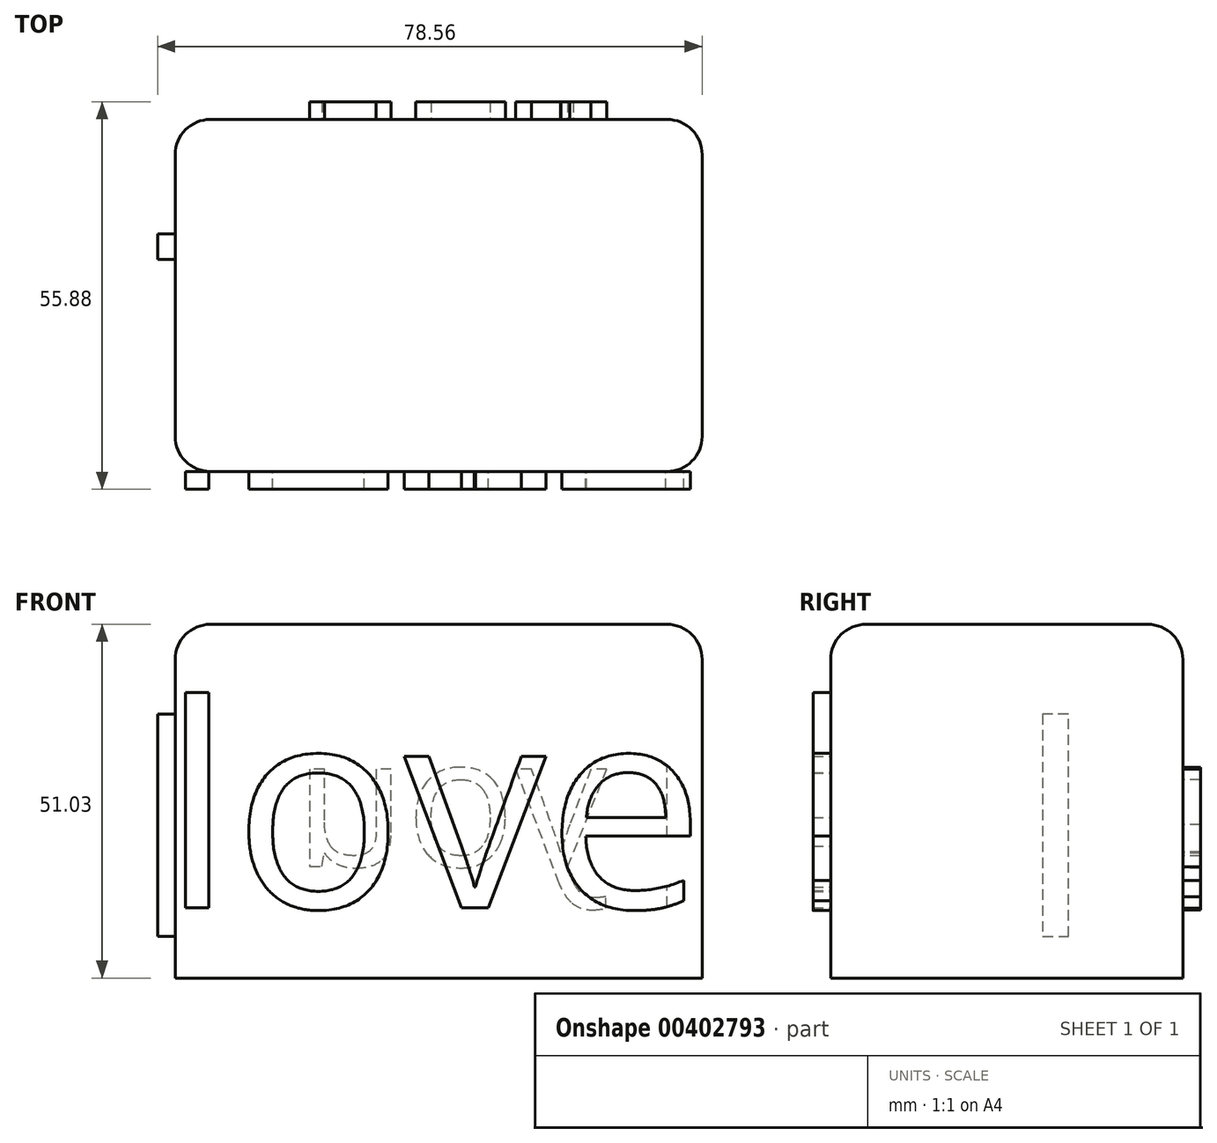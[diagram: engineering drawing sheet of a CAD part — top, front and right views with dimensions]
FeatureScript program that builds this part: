
annotation { "Feature Type Name" : "Feature", "Feature Type Description" : "" }
export const myFeature = defineFeature(function(context is Context, id is Id, definition is map)
    precondition{}
    {
        {
            var Q0;
            Q0=qCreatedBy(makeId("Front.planeOp"),FACE);
            var sketch = newSketch(context, id + "F0", { "sketchPlane" : qUnion([Q0])});
            skLineSegment(sketch, "E0.bottom", {"start": v(0, 0) * mm, "end": v(76.02, 0) * mm});
            skLineSegment(sketch, "E0.top", {"start": v(0, 51.03) * mm, "end": v(76.02, 51.03) * mm});
            skLineSegment(sketch, "E0.left", {"start": v(0, 0) * mm, "end": v(0, 51.03) * mm});
            skLineSegment(sketch, "E0.right", {"start": v(76.02, 0) * mm, "end": v(76.02, 51.03) * mm});
            skSolve(sketch);
        }
        {
            var Q0;
            Q0=makeQuery(id+"F0.imprint","IMPRINT",FACE,{"disambiguationData":[TD([[makeQuery(id+"F0.imprint","IMPRINT",EDGE,{"derivedFrom":sQuery(id+"F0.wireOp",EDGE,"E0.bottom")}),1.0]])]});
            extrude(context, id + "F1", {"entities" : qUnion([Q0]), "depth" : 50.8 * mm});
        }
        {
            var Q0;
            Q0=makeQuery(id+"F1.opExtrude","CAP_EDGE",EDGE,{"disambiguationData":[OSD([sQuery(id+"F0.wireOp",EDGE,"E0.top")])],"isStart":false});
            fillet(context, id + "F2", {"entities" : qUnion([Q0]), "radius" : 5.08 * mm, "tangentPropagation" : true, "allowEdgeOverflow" : false});
        }
        {
            var Q0;
            Q0=makeQuery(id+"F1.opExtrude","SWEPT_EDGE",EDGE,{"disambiguationData":[OSD([sQuery(id+"F0.wireOp",EDGE,"E0.top"),sQuery(id+"F0.wireOp",EDGE,"E0.right")])]});
            fillet(context, id + "F3", {"entities" : qUnion([Q0]), "radius" : 5.08 * mm, "tangentPropagation" : true, "allowEdgeOverflow" : false});
        }
        {
            var Q0;
            Q0=makeQuery(id+"F1.opExtrude","CAP_EDGE",EDGE,{"disambiguationData":[OSD([sQuery(id+"F0.wireOp",EDGE,"E0.top")])],"isStart":true});
            fillet(context, id + "F4", {"entities" : qUnion([Q0]), "radius" : 5.08 * mm, "tangentPropagation" : true, "allowEdgeOverflow" : false});
        }
        {
            var Q0;
            Q0=makeQuery(id+"F1.opExtrude","SWEPT_EDGE",EDGE,{"disambiguationData":[OSD([sQuery(id+"F0.wireOp",EDGE,"E0.top"),sQuery(id+"F0.wireOp",EDGE,"E0.left")])]});
            fillet(context, id + "F5", {"entities" : qUnion([Q0]), "radius" : 5.08 * mm, "tangentPropagation" : true, "allowEdgeOverflow" : false});
        }
        {
            var Q0;
            Q0=makeQuery(id+"F1.opExtrude","SWEPT_FACE",FACE,{"disambiguationData":[OSD([sQuery(id+"F0.wireOp",EDGE,"E0.left")])]});
            var sketch = newSketch(context, id + "F6", { "sketchPlane" : qUnion([Q0])});
            skText(sketch, "E1", { "text": "I", "fontName": "OpenSans-Regular.ttf"});
            const initialGuessF6  = {"E1": [0.01208, 0.006, 1, 0, 0.03235]};
            skSetInitialGuess(sketch, initialGuessF6);
            skSolve(sketch);
        }
        {
            var Q0;
            Q0 = qSketchRegion(id + "F6", true);
            extrude(context, id + "F7", {"entities" : qUnion([Q0]), "operationType" : NewBodyOperationType.ADD, "depth" : 2.54 * mm});
        }
        {
            var Q0;
            Q0=makeQuery(id+"F1.opExtrude","CAP_FACE",FACE,{"disambiguationData":[OSD([sQuery(id+"F0.wireOp",EDGE,"E0.bottom"),sQuery(id+"F0.wireOp",EDGE,"E0.top"),sQuery(id+"F0.wireOp",EDGE,"E0.left"),sQuery(id+"F0.wireOp",EDGE,"E0.right")])],"isStart":false});
            var sketch = newSketch(context, id + "F8", { "sketchPlane" : qUnion([Q0])});
            skText(sketch, "E2", { "text": "love", "fontName": "OpenSans-Regular.ttf"});
            const initialGuessF8  = {"E2": [-0.00201, 0.01013, 1, 0, 0.02943]};
            skSetInitialGuess(sketch, initialGuessF8);
            skSolve(sketch);
        }
        {
            var Q0;
            Q0 = qSketchRegion(id + "F8", true);
            extrude(context, id + "F9", {"entities" : qUnion([Q0]), "operationType" : NewBodyOperationType.ADD, "depth" : 2.54 * mm});
        }
        {
            var Q0;
            Q0=makeQuery(id+"F1.opExtrude","CAP_FACE",FACE,{"disambiguationData":[OSD([sQuery(id+"F0.wireOp",EDGE,"E0.bottom"),sQuery(id+"F0.wireOp",EDGE,"E0.top"),sQuery(id+"F0.wireOp",EDGE,"E0.left"),sQuery(id+"F0.wireOp",EDGE,"E0.right")])],"isStart":true});
            var sketch = newSketch(context, id + "F10", { "sketchPlane" : qUnion([Q0])});
            skText(sketch, "E3", { "text": "you", "fontName": "OpenSans-Regular.ttf"});
            const initialGuessF10  = {"E3": [-0.0623, 0.01613, 1, 0, 0.01888]};
            skSetInitialGuess(sketch, initialGuessF10);
            skSolve(sketch);
        }
        {
            var Q0;
            Q0 = qSketchRegion(id + "F10", true);
            extrude(context, id + "F11", {"entities" : qUnion([Q0]), "operationType" : NewBodyOperationType.ADD, "depth" : 2.54 * mm});
        }
    });
